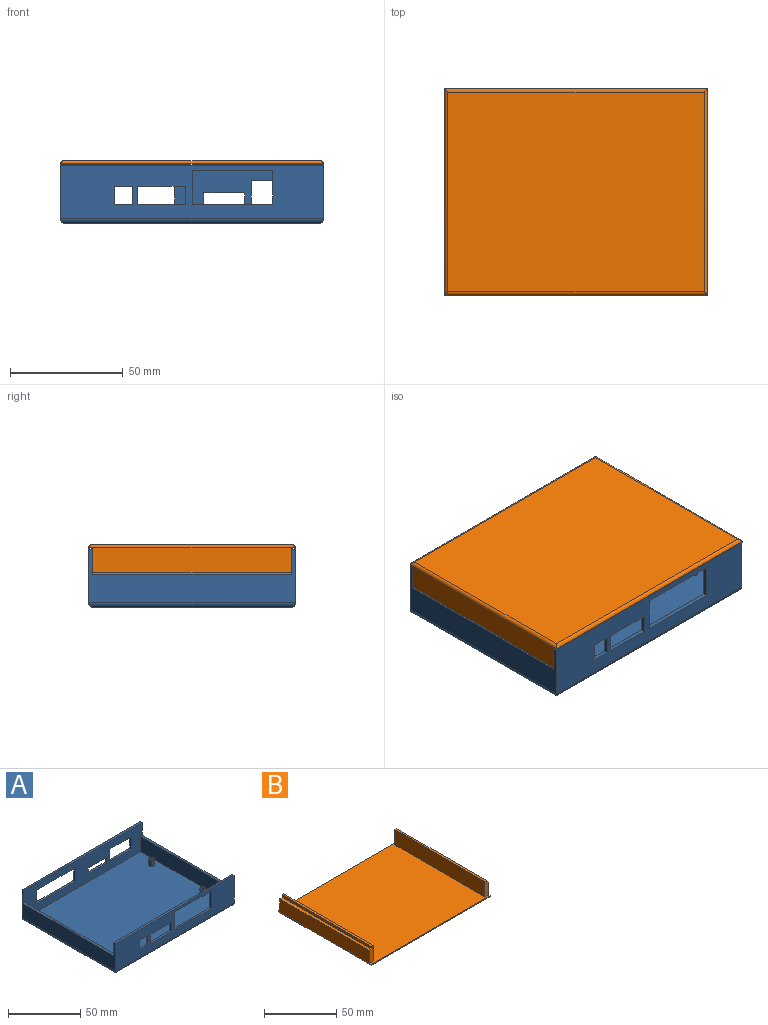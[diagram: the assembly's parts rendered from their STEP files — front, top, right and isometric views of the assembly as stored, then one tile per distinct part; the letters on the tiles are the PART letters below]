
ASSEMBLY  parts=2 mates=1
PART A: 58 faces, bbox 116.4x91.5x25.7 mm
  f0: plane 116.4x1.7mm, normal (0,0,1), area 197.9mm2, adj f1,f2,f3,f7
  f1: plane 91.5x23.7mm, normal (1,0,0), area 1199.5mm2, adj f0,f2,f3,f4,f5,f6,f47,f48
  f2: plane 116.4x23.7mm, normal (0,1,0), area 2011.2mm2, adj f0,f1,f7,f24,f25,f26,f27,f28
  f3: plane 116.4x24mm, normal (0,-1,0), area 2001.9mm2, adj f0,f1,f7,f9,f10,f11,f24,f25
  f4: plane 116.4x23.7mm, normal (0,-1,0), area 1991.2mm2, adj f1,f6,f7,f12,f13,f14,f15,f16
  f5: plane 116.4x24mm, normal (0,1,0), area 1981.9mm2, adj f1,f6,f7,f9,f10,f11,f12,f13
  f6: plane 116.4x1.7mm, normal (0,0,1), area 197.9mm2, adj f1,f4,f5,f7
  f7: plane 91.5x23.7mm, normal (-1,0,0), area 1199.4mm2, adj f0,f2,f3,f4,f5,f6,f44,f49
  f8: plane 112.4x87.5mm, normal (0,0,-1), area 9835mm2, adj f44,f45,f46,f47
  f9: plane 88.1x13mm, normal (1,0,0), area 1145.3mm2, adj f3,f5,f11,f49
  f10: plane 88.1x13mm, normal (-1,0,0), area 1145.3mm2, adj f3,f5,f11,f48
  f11: plane 113x88.1mm, normal (0,0,1), area 9905mm2, adj f3,f5,f9,f10,f36,f38,f40,f42
  f12: plane 15x1.7mm, normal (1,0,0), area 25.5mm2, adj f4,f5,f13,f15
  f13: plane 35.7x1.7mm, normal (0,0,1), area 60.7mm2, adj f4,f5,f12,f14
  f14: plane 15x1.7mm, normal (-1,0,0), area 25.5mm2, adj f4,f5,f13,f15
  f15: plane 35.7x1.7mm, normal (0,0,-1), area 60.7mm2, adj f4,f5,f12,f14
  f16: plane 21x1.7mm, normal (0,0,1), area 35.7mm2, adj f4,f5,f17,f19
  f17: plane 8x1.7mm, normal (-1,0,0), area 13.6mm2, adj f4,f5,f16,f18
  f18: plane 21x1.7mm, normal (0,0,-1), area 35.7mm2, adj f4,f5,f17,f19
  f19: plane 8x1.7mm, normal (1,0,0), area 13.6mm2, adj f4,f5,f16,f18
  f20: plane 8x1.7mm, normal (1,0,0), area 13.6mm2, adj f4,f5,f21,f23
  f21: plane 8x1.7mm, normal (0,0,1), area 13.6mm2, adj f4,f5,f20,f22
  f22: plane 8x1.7mm, normal (-1,0,0), area 13.6mm2, adj f4,f5,f21,f23
  f23: plane 8x1.7mm, normal (0,0,-1), area 13.6mm2, adj f4,f5,f20,f22
  f24: plane 21x1.7mm, normal (0,0,1), area 35.7mm2, adj f2,f3,f25,f27
  f25: plane 10.5x1.7mm, normal (1,0,0), area 17.9mm2, adj f2,f3,f24,f26
  f26: plane 21x1.7mm, normal (0,0,-1), area 35.7mm2, adj f2,f3,f25,f27
  f27: plane 10.5x1.7mm, normal (-1,0,0), area 17.9mm2, adj f2,f3,f24,f26
  f28: plane 5x1.7mm, normal (-1,0,0), area 8.5mm2, adj f2,f3,f29,f31
  f29: plane 18x1.7mm, normal (0,0,1), area 30.6mm2, adj f2,f3,f28,f30
  f30: plane 5x1.7mm, normal (1,0,0), area 8.5mm2, adj f2,f3,f29,f31
  f31: plane 18x1.7mm, normal (0,0,-1), area 30.6mm2, adj f2,f3,f28,f30
  f32: plane 38x1.7mm, normal (0,0,1), area 64.6mm2, adj f2,f3,f33,f35
  f33: plane 11.5x1.7mm, normal (1,0,0), area 19.6mm2, adj f2,f3,f32,f34
  f34: plane 38x1.7mm, normal (0,0,-1), area 64.6mm2, adj f2,f3,f33,f35
  f35: plane 11.5x1.7mm, normal (-1,0,0), area 19.6mm2, adj f2,f3,f32,f34
  f36: cylinder r=2mm len=5mm, axis (0,0,-1), area 62.8mm2, adj f11,f37
  f37: plane 4x4mm, normal (0,0,1), area 7.7mm2, adj f36,f56
  f38: cylinder r=2mm len=5mm, axis (0,0,-1), area 62.8mm2, adj f11,f39
  f39: plane 4x4mm, normal (0,0,1), area 7.7mm2, adj f38,f54
  f40: cylinder r=2mm len=5mm, axis (0,0,-1), area 62.8mm2, adj f11,f41
  f41: plane 4x4mm, normal (0,0,1), area 7.7mm2, adj f40,f52
  f42: cylinder r=2mm len=5mm, axis (0,0,-1), area 62.8mm2, adj f11,f43
  f43: plane 4x4mm, normal (0,0,1), area 7.7mm2, adj f42,f50
  f44: cylinder r=2mm len=91.5mm, axis (0,-1,0), area 282.9mm2, adj f7,f8,f45,f46
  f45: cylinder r=2mm len=116.4mm, axis (1,0,0), area 361.1mm2, adj f4,f8,f44,f47
  f46: cylinder r=2mm len=116.4mm, axis (-1,0,0), area 361.1mm2, adj f2,f8,f44,f47
  f47: cylinder r=2mm len=91.5mm, axis (0,1,0), area 282.9mm2, adj f1,f8,f45,f46
  f48: plane 88.1x1.7mm, normal (0,0,1), area 149.8mm2, adj f1,f3,f5,f10
  f49: plane 88.1x1.7mm, normal (0,0,1), area 149.8mm2, adj f3,f5,f7,f9
  f50: cylinder r=1.25mm len=5mm, axis (0,0,-1), area 39.3mm2, adj f43,f51
  f51: plane 2.5x2.5mm, normal (0,0,1), area 4.9mm2, adj f50
  f52: cylinder r=1.25mm len=5mm, axis (0,0,-1), area 39.3mm2, adj f41,f53
  f53: plane 2.5x2.5mm, normal (0,0,1), area 4.9mm2, adj f52
  f54: cylinder r=1.25mm len=5mm, axis (0,0,-1), area 39.3mm2, adj f39,f55
  f55: plane 2.5x2.5mm, normal (0,0,1), area 4.9mm2, adj f54
  f56: cylinder r=1.25mm len=5mm, axis (0,0,-1), area 39.3mm2, adj f37,f57
  f57: plane 2.5x2.5mm, normal (0,0,1), area 4.9mm2, adj f56
PART B: 22 faces, bbox 116.4x91.5x14.7 mm
  f0: plane 116.4x91.5mm, normal (0,0,1), area 9989.8mm2, adj f1,f2,f3,f4,f6,f7,f9,f10
  f1: plane 91.5x11mm, normal (1,0,0), area 969.8mm2, adj f0,f2,f4,f9,f10,f11,f12
  f2: plane 116.4x0.2mm, normal (0,1,0), area 23.3mm2, adj f0,f1,f3,f13
  f3: plane 91.5x11mm, normal (-1,0,0), area 969.8mm2, adj f0,f2,f4,f6,f7,f8,f15
  f4: plane 116.4x0.2mm, normal (0,-1,0), area 23.3mm2, adj f0,f1,f3,f14
  f5: plane 113.4x88.5mm, normal (0,0,-1), area 10035.9mm2, adj f12,f13,f14,f15
  f6: plane 13x4.1mm, normal (0,-1,0), area 48mm2, adj f0,f3,f8,f16,f17,f18
  f7: plane 13x4.1mm, normal (0,1,0), area 48mm2, adj f0,f3,f8,f16,f17,f18
  f8: plane 88.1x2.4mm, normal (0,0,1), area 211.4mm2, adj f3,f6,f7,f16
  f9: plane 13x3.4mm, normal (0,-1,0), area 40.5mm2, adj f0,f1,f11,f19,f20,f21
  f10: plane 13x3.4mm, normal (0,1,0), area 40.5mm2, adj f0,f1,f11,f19,f20,f21
  f11: plane 88.1x1.7mm, normal (0,0,1), area 149.8mm2, adj f1,f9,f10,f19
  f12: cylinder r=1.5mm len=91.5mm, axis (0,1,0), area 213mm2, adj f1,f5,f13,f14
  f13: cylinder r=1.5mm len=116.4mm, axis (-1,0,0), area 271.7mm2, adj f2,f5,f12,f15
  f14: cylinder r=1.5mm len=116.4mm, axis (1,0,0), area 271.7mm2, adj f4,f5,f12,f15
  f15: cylinder r=1.5mm len=91.5mm, axis (0,-1,0), area 213mm2, adj f3,f5,f13,f14
  f16: plane 88.1x2.2mm, normal (-1,0,0), area 193.8mm2, adj f6,f7,f8,f18
  f17: plane 88.1x13mm, normal (1,0,0), area 1145.3mm2, adj f0,f6,f7,f18
  f18: plane 88.1x1.7mm, normal (0,0,1), area 149.8mm2, adj f6,f7,f16,f17
  f19: plane 88.1x2.2mm, normal (1,0,0), area 193.8mm2, adj f9,f10,f11,f21
  f20: plane 88.1x13mm, normal (-1,0,0), area 1145.3mm2, adj f0,f9,f10,f21
  f21: plane 88.1x1.7mm, normal (0,0,1), area 149.8mm2, adj f9,f10,f19,f20
PLACE A at identity fixed
PLACE B rot(axis=(1,0,0),180deg) t=(0,-15.49,26.13)mm
MATE slider B.f0 <-> A.f6  axis (0,0,-1) through (-1.7,-1.7,24.43)mm
